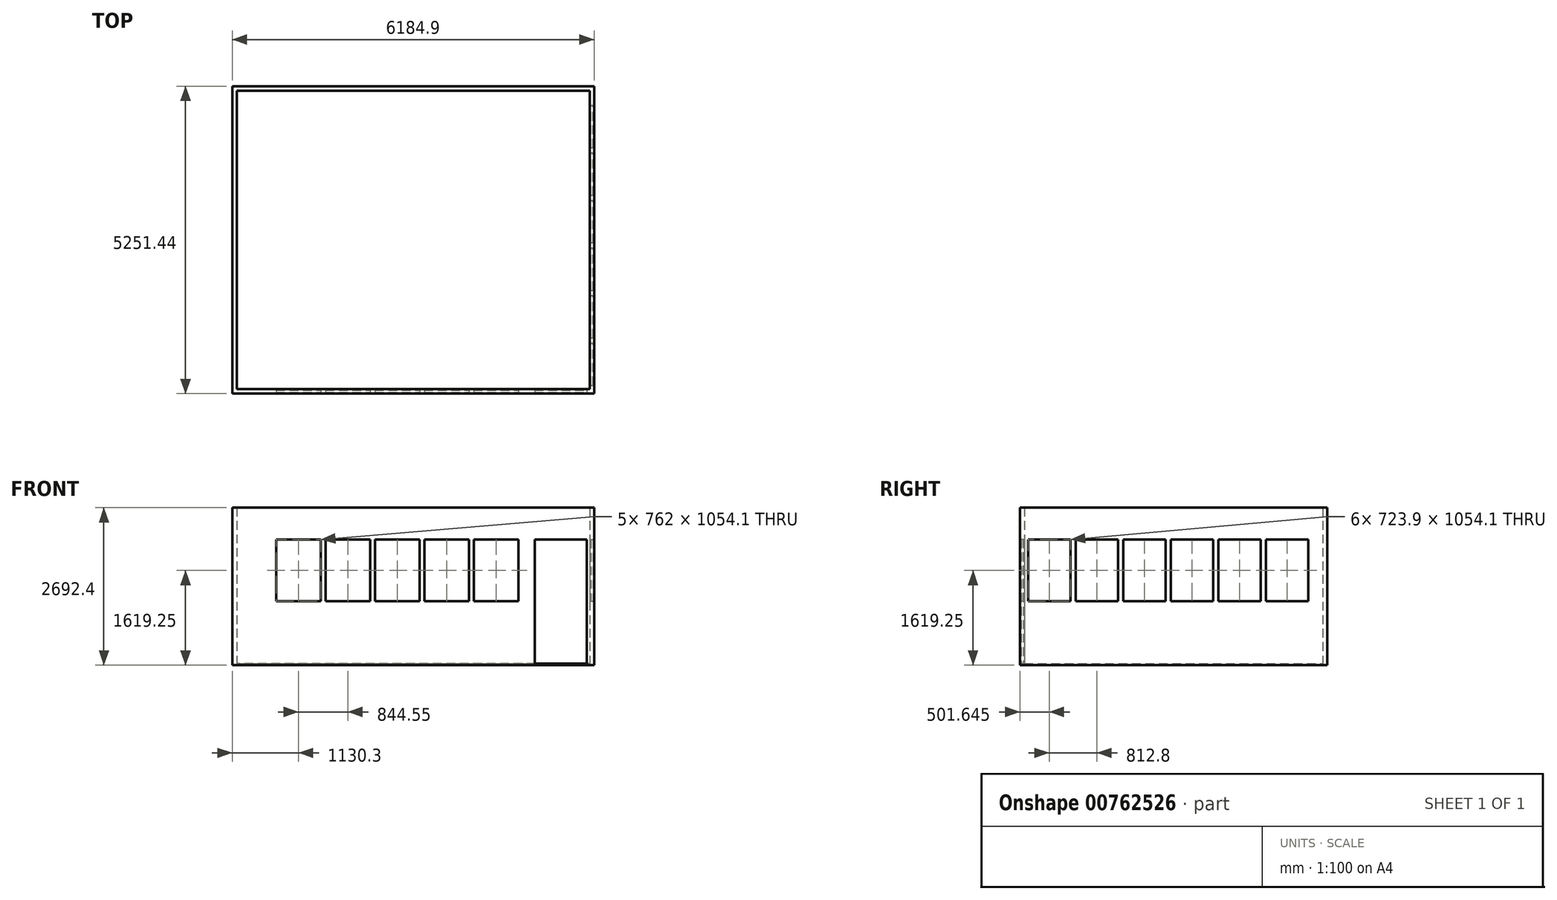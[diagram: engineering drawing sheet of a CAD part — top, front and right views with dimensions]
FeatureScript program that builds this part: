
annotation { "Feature Type Name" : "Feature", "Feature Type Description" : "" }
export const myFeature = defineFeature(function(context is Context, id is Id, definition is map)
    precondition{}
    {
        {
            var Q0;
            Q0=qCreatedBy(makeId("Top.planeOp"),FACE);
            var sketch = newSketch(context, id + "F0", { "sketchPlane" : qUnion([Q0])});
            skLineSegment(sketch, "E0.bottom", {"start": v(-3092.45, 2625.73) * mm, "end": v(3092.45, 2625.72) * mm});
            skLineSegment(sketch, "E0.top", {"start": v(-3092.45, -2625.72) * mm, "end": v(3092.45, -2625.73) * mm});
            skLineSegment(sketch, "E0.left", {"start": v(-3092.45, 2625.72) * mm, "end": v(-3092.45, -2625.72) * mm});
            skLineSegment(sketch, "E0.right", {"start": v(3092.45, 2625.72) * mm, "end": v(3092.45, -2625.72) * mm});
            skSolve(sketch);
        }
        {
            var Q0;
            Q0 = qSketchRegion(id + "F0", true);
            extrude(context, id + "F1", {"entities" : qUnion([Q0]), "depth" : 25.4 * mm, "offsetDistance" : 25.4 * mm});
        }
        {
            var Q0;
            Q0=makeQuery(id+"F1.opExtrude","CAP_FACE",FACE,{"disambiguationData":[OSD([sQuery(id+"F0.wireOp",EDGE,"E0.bottom"),sQuery(id+"F0.wireOp",EDGE,"E0.top"),sQuery(id+"F0.wireOp",EDGE,"E0.left"),sQuery(id+"F0.wireOp",EDGE,"E0.right")])],"isStart":false});
            var sketch = newSketch(context, id + "F2", { "sketchPlane" : qUnion([Q0])});
            skLineSegment(sketch, "E1.0", {"start": v(-3092.45, 2625.73) * mm, "end": v(-3092.45, -2625.72) * mm});
            skLineSegment(sketch, "E1.1", {"start": v(3092.45, 2625.72) * mm, "end": v(-3092.45, 2625.73) * mm});
            skLineSegment(sketch, "E1.2", {"start": v(3092.45, -2625.73) * mm, "end": v(3092.45, 2625.72) * mm});
            skLineSegment(sketch, "E1.3", {"start": v(-3092.45, -2625.72) * mm, "end": v(3092.45, -2625.73) * mm});
            skLineSegment(sketch, "E2.0", {"start": v(-3016.25, 2549.53) * mm, "end": v(-3016.25, -2549.52) * mm});
            skLineSegment(sketch, "E2.1", {"start": v(3016.25, 2549.52) * mm, "end": v(-3016.25, 2549.53) * mm});
            skLineSegment(sketch, "E2.2", {"start": v(3016.25, -2549.53) * mm, "end": v(3016.25, 2549.52) * mm});
            skLineSegment(sketch, "E2.3", {"start": v(-3016.25, -2549.52) * mm, "end": v(3016.25, -2549.53) * mm});
            skSolve(sketch);
        }
        {
            var Q0;
            Q0 = qSketchRegion(id + "F2", true);
            extrude(context, id + "F3", {"entities" : qUnion([Q0]), "operationType" : NewBodyOperationType.ADD, "depth" : 2667 * mm, "offsetDistance" : 25.4 * mm});
        }
        {
            var Q0;
            Q0=makeQuery(id+"F3.boolean.opBoolean","MERGE",FACE,{"derivedFrom":[makeQuery(id+"F1.opExtrude","SWEPT_FACE",FACE,{"disambiguationData":[OSD([sQuery(id+"F0.wireOp",EDGE,"E0.top")])]}),makeQuery(id+"F3.opExtrude","SWEPT_FACE",FACE,{"disambiguationData":[OSD([sQuery(id+"F2.wireOp",EDGE,"E1.3")])]})]});
            var sketch = newSketch(context, id + "F4", { "sketchPlane" : qUnion([Q0])});
            skLineSegment(sketch, "E3.bottom", {"start": v(2076.45, 2146.3) * mm, "end": v(2965.45, 2146.3) * mm});
            skLineSegment(sketch, "E3.top", {"start": v(2076.45, 25.4) * mm, "end": v(2965.45, 25.4) * mm});
            skLineSegment(sketch, "E3.left", {"start": v(2076.45, 2146.3) * mm, "end": v(2076.45, 25.4) * mm});
            skLineSegment(sketch, "E3.right", {"start": v(2965.45, 2146.3) * mm, "end": v(2965.45, 25.4) * mm});
            skSolve(sketch);
        }
        {
            var Q0;
            Q0 = qSketchRegion(id + "F4", true);
            extrude(context, id + "F5", {"entities" : qUnion([Q0]), "operationType" : NewBodyOperationType.REMOVE, "oppositeDirection" : true, "depth" : 76.2 * mm, "offsetDistance" : 25.4 * mm});
        }
        {
            var Q0;
            Q0=makeQuery(id+"F3.boolean.opBoolean","MERGE",FACE,{"derivedFrom":[makeQuery(id+"F1.opExtrude","SWEPT_FACE",FACE,{"disambiguationData":[OSD([sQuery(id+"F0.wireOp",EDGE,"E0.right")])]}),makeQuery(id+"F3.opExtrude","SWEPT_FACE",FACE,{"disambiguationData":[OSD([sQuery(id+"F2.wireOp",EDGE,"E1.2")])]})]});
            var sketch = newSketch(context, id + "F6", { "sketchPlane" : qUnion([Q0])});
            skLineSegment(sketch, "E4", {"start": v(-2486.02, 2146.3) * mm, "end": v(-1762.12, 2146.3) * mm});
            skLineSegment(sketch, "E5", {"start": v(-2486.02, 2146.3) * mm, "end": v(-2486.02, 1092.2) * mm});
            skLineSegment(sketch, "E6", {"start": v(-2486.02, 1092.2) * mm, "end": v(-1762.12, 1092.2) * mm});
            skLineSegment(sketch, "E7", {"start": v(-1762.12, 2146.3) * mm, "end": v(-1762.12, 1092.2) * mm});
            skLineSegment(sketch, "E8", {"start": v(-1762.12, 2146.3) * mm, "end": v(-1673.22, 2146.3) * mm, "construction": true});
            skLineSegment(sketch, "E9", {"start": v(-1673.22, 2146.3) * mm, "end": v(-949.32, 2146.3) * mm});
            skLineSegment(sketch, "E10", {"start": v(-949.32, 2146.3) * mm, "end": v(-860.42, 2146.3) * mm, "construction": true});
            skLineSegment(sketch, "E11", {"start": v(-860.42, 2146.3) * mm, "end": v(-136.52, 2146.3) * mm});
            skLineSegment(sketch, "E12", {"start": v(-136.52, 2146.3) * mm, "end": v(-47.62, 2146.3) * mm, "construction": true});
            skLineSegment(sketch, "E13", {"start": v(-47.62, 2146.3) * mm, "end": v(676.28, 2146.3) * mm});
            skLineSegment(sketch, "E14", {"start": v(676.28, 2146.3) * mm, "end": v(765.18, 2146.3) * mm, "construction": true});
            skLineSegment(sketch, "E15", {"start": v(765.18, 2146.3) * mm, "end": v(1489.08, 2146.3) * mm});
            skLineSegment(sketch, "E16", {"start": v(1489.08, 2146.3) * mm, "end": v(1577.98, 2146.3) * mm, "construction": true});
            skLineSegment(sketch, "E17", {"start": v(1577.98, 2146.3) * mm, "end": v(2301.88, 2146.3) * mm});
            skLineSegment(sketch, "E18", {"start": v(2301.88, 2146.3) * mm, "end": v(2301.88, 1092.2) * mm});
            skLineSegment(sketch, "E19", {"start": v(1577.98, 2146.3) * mm, "end": v(1577.98, 1092.2) * mm});
            skLineSegment(sketch, "E20", {"start": v(1489.08, 2146.3) * mm, "end": v(1489.08, 1092.2) * mm});
            skLineSegment(sketch, "E21", {"start": v(765.18, 2146.3) * mm, "end": v(765.18, 1092.2) * mm});
            skLineSegment(sketch, "E22", {"start": v(676.28, 2146.3) * mm, "end": v(676.28, 1092.2) * mm});
            skLineSegment(sketch, "E23", {"start": v(-47.62, 2146.3) * mm, "end": v(-47.62, 1092.2) * mm});
            skLineSegment(sketch, "E24", {"start": v(-136.52, 2146.3) * mm, "end": v(-136.52, 1092.2) * mm});
            skLineSegment(sketch, "E25", {"start": v(-860.42, 2146.3) * mm, "end": v(-860.42, 1092.2) * mm});
            skLineSegment(sketch, "E26", {"start": v(-949.32, 2146.3) * mm, "end": v(-949.32, 1092.2) * mm});
            skLineSegment(sketch, "E27", {"start": v(-1673.22, 2146.3) * mm, "end": v(-1673.22, 1092.2) * mm});
            skLineSegment(sketch, "E28.trimOffspring", {"start": v(-1673.22, 1092.2) * mm, "end": v(-949.32, 1092.2) * mm});
            skLineSegment(sketch, "E29.trimOffspring", {"start": v(-860.42, 1092.2) * mm, "end": v(-136.52, 1092.2) * mm});
            skLineSegment(sketch, "E30.trimOffspring", {"start": v(-47.62, 1092.2) * mm, "end": v(676.28, 1092.2) * mm});
            skLineSegment(sketch, "E31.trimOffspring", {"start": v(765.18, 1092.2) * mm, "end": v(1489.08, 1092.2) * mm});
            skLineSegment(sketch, "E32.trimOffspring", {"start": v(1577.98, 1092.2) * mm, "end": v(2301.88, 1092.2) * mm});
            skSolve(sketch);
        }
        {
            var Q0;
            Q0 = qSketchRegion(id + "F6", true);
            extrude(context, id + "F7", {"entities" : qUnion([Q0]), "operationType" : NewBodyOperationType.REMOVE, "oppositeDirection" : true, "depth" : 76.2 * mm, "offsetDistance" : 25.4 * mm});
        }
        {
            var Q0;
            Q0=makeQuery(id+"F3.boolean.opBoolean","MERGE",FACE,{"derivedFrom":[makeQuery(id+"F1.opExtrude","SWEPT_FACE",FACE,{"disambiguationData":[OSD([sQuery(id+"F0.wireOp",EDGE,"E0.top")])]}),makeQuery(id+"F3.opExtrude","SWEPT_FACE",FACE,{"disambiguationData":[OSD([sQuery(id+"F2.wireOp",EDGE,"E1.3")])]})]});
            var sketch = newSketch(context, id + "F8", { "sketchPlane" : qUnion([Q0])});
            skLineSegment(sketch, "E33.bottom", {"start": v(-2343.15, 1092.2) * mm, "end": v(-1581.15, 1092.2) * mm});
            skLineSegment(sketch, "E33.top", {"start": v(-2343.15, 2146.3) * mm, "end": v(-1581.15, 2146.3) * mm});
            skLineSegment(sketch, "E33.left", {"start": v(-2343.15, 1092.2) * mm, "end": v(-2343.15, 2146.3) * mm});
            skLineSegment(sketch, "E33.right", {"start": v(-1581.15, 1092.2) * mm, "end": v(-1581.15, 2146.3) * mm});
            skLineSegment(sketch, "E34", {"start": v(-1581.15, 2146.3) * mm, "end": v(-1498.6, 2146.3) * mm, "construction": true});
            skLineSegment(sketch, "E35", {"start": v(-1498.6, 2146.3) * mm, "end": v(-736.6, 2146.3) * mm});
            skLineSegment(sketch, "E36", {"start": v(-736.6, 2146.3) * mm, "end": v(-654.05, 2146.3) * mm, "construction": true});
            skLineSegment(sketch, "E37", {"start": v(-654.05, 2146.3) * mm, "end": v(107.95, 2146.3) * mm});
            skLineSegment(sketch, "E38", {"start": v(107.95, 2146.3) * mm, "end": v(190.5, 2146.3) * mm, "construction": true});
            skLineSegment(sketch, "E39", {"start": v(190.5, 2146.3) * mm, "end": v(952.5, 2146.3) * mm});
            skLineSegment(sketch, "E40", {"start": v(952.5, 2146.3) * mm, "end": v(1035.05, 2146.3) * mm, "construction": true});
            skLineSegment(sketch, "E41", {"start": v(1035.05, 2146.3) * mm, "end": v(1797.05, 2146.3) * mm});
            skLineSegment(sketch, "E42", {"start": v(-1498.6, 1092.2) * mm, "end": v(-736.6, 1092.2) * mm});
            skLineSegment(sketch, "E43", {"start": v(1797.05, 2146.3) * mm, "end": v(1797.05, 1092.2) * mm});
            skLineSegment(sketch, "E44", {"start": v(1035.05, 2146.3) * mm, "end": v(1035.05, 1092.2) * mm});
            skLineSegment(sketch, "E45", {"start": v(952.5, 2146.3) * mm, "end": v(952.5, 1092.2) * mm});
            skLineSegment(sketch, "E46", {"start": v(190.5, 2146.3) * mm, "end": v(190.5, 1092.2) * mm});
            skLineSegment(sketch, "E47", {"start": v(107.95, 2146.3) * mm, "end": v(107.95, 1092.2) * mm});
            skLineSegment(sketch, "E48", {"start": v(-654.05, 2146.3) * mm, "end": v(-654.05, 1092.2) * mm});
            skLineSegment(sketch, "E49", {"start": v(-736.6, 2146.3) * mm, "end": v(-736.6, 1092.2) * mm});
            skLineSegment(sketch, "E50", {"start": v(-1498.6, 2146.3) * mm, "end": v(-1498.6, 1092.2) * mm});
            skLineSegment(sketch, "E51.trimOffspring", {"start": v(-654.05, 1092.2) * mm, "end": v(107.95, 1092.2) * mm});
            skLineSegment(sketch, "E52.trimOffspring", {"start": v(190.5, 1092.2) * mm, "end": v(952.5, 1092.2) * mm});
            skLineSegment(sketch, "E53.trimOffspring", {"start": v(1035.05, 1092.2) * mm, "end": v(1797.05, 1092.2) * mm});
            skSolve(sketch);
        }
        {
            var Q0;
            Q0 = qSketchRegion(id + "F8", true);
            extrude(context, id + "F9", {"entities" : qUnion([Q0]), "operationType" : NewBodyOperationType.REMOVE, "oppositeDirection" : true, "depth" : 76.2 * mm, "offsetDistance" : 25.4 * mm});
        }
        {
            var Q0;
            Q0 = qSketchRegion(id + "F4", true);
            extrude(context, id + "F10", {"entities" : qUnion([Q0]), "oppositeDirection" : true, "depth" : 57.15 * mm, "offsetDistance" : 25.4 * mm, "hasSecondDirection" : true, "secondDirectionOppositeDirection" : true, "secondDirectionDepth" : 19.05 * mm});
        }
        {
            var Q0;
            Q0 = qSketchRegion(id + "F6", true);
            extrude(context, id + "F11", {"entities" : qUnion([Q0]), "oppositeDirection" : true, "depth" : 57.15 * mm, "offsetDistance" : 25.4 * mm, "hasSecondDirection" : true, "secondDirectionOppositeDirection" : true, "secondDirectionDepth" : 19.05 * mm});
        }
        {
            var Q0;
            Q0 = qSketchRegion(id + "F8", true);
            extrude(context, id + "F12", {"entities" : qUnion([Q0]), "oppositeDirection" : true, "depth" : 57.15 * mm, "offsetDistance" : 25.4 * mm, "hasSecondDirection" : true, "secondDirectionOppositeDirection" : true, "secondDirectionDepth" : 19.05 * mm});
        }
    });
